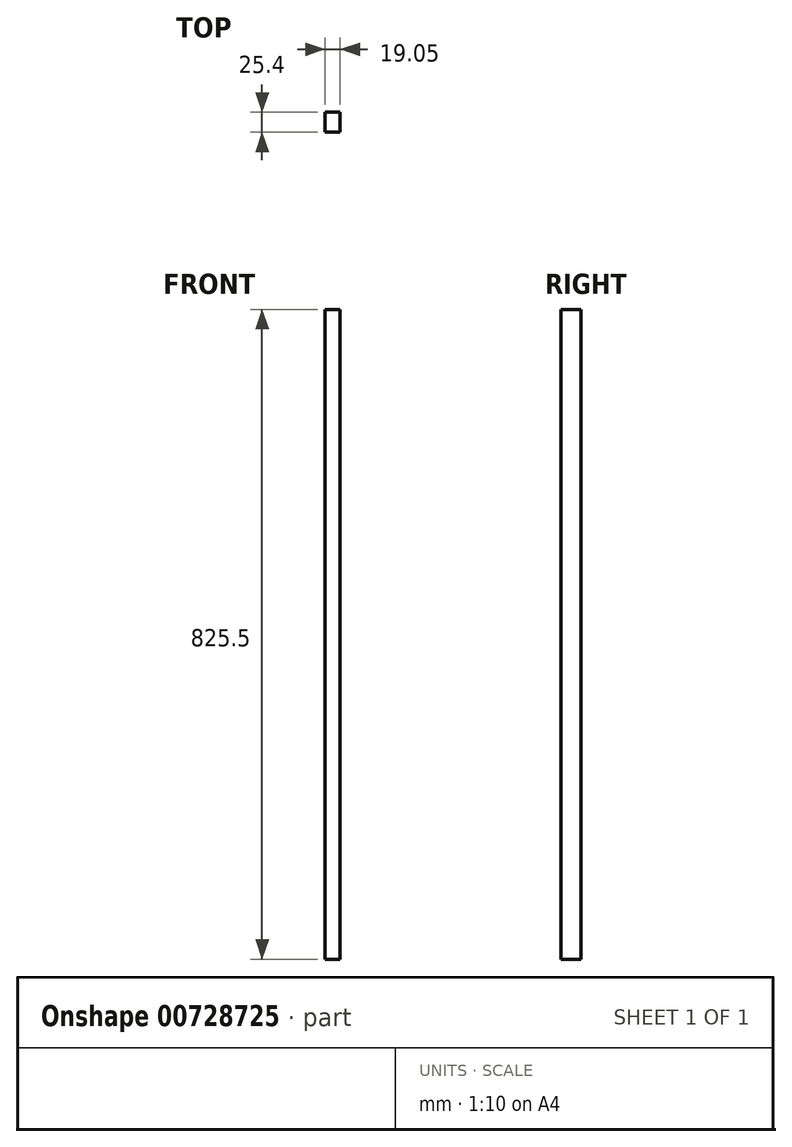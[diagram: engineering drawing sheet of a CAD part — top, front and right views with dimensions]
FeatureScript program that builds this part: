
annotation { "Feature Type Name" : "Feature", "Feature Type Description" : "" }
export const myFeature = defineFeature(function(context is Context, id is Id, definition is map)
    precondition{}
    {
        {
            var Q0;
            Q0=qCreatedBy(makeId("Right.planeOp"),FACE);
            var sketch = newSketch(context, id + "F0", { "sketchPlane" : qUnion([Q0])});
            skLineSegment(sketch, "E0.bottom", {"start": v(12.7, 412.75) * mm, "end": v(-12.7, 412.75) * mm});
            skLineSegment(sketch, "E0.top", {"start": v(12.7, -412.75) * mm, "end": v(-12.7, -412.75) * mm});
            skLineSegment(sketch, "E0.left", {"start": v(12.7, 412.75) * mm, "end": v(12.7, -412.75) * mm});
            skLineSegment(sketch, "E0.right", {"start": v(-12.7, 412.75) * mm, "end": v(-12.7, -412.75) * mm});
            skPoint(sketch, "E0.middle", {"position": v(0, 0) * mm});
            skSolve(sketch);
        }
        {
            var Q0;
            Q0 = qSketchRegion(id + "F0", true);
            extrude(context, id + "F1", {"entities" : qUnion([Q0]), "depth" : 19.05 * mm, "offsetDistance" : 25.4 * mm});
        }
    });
